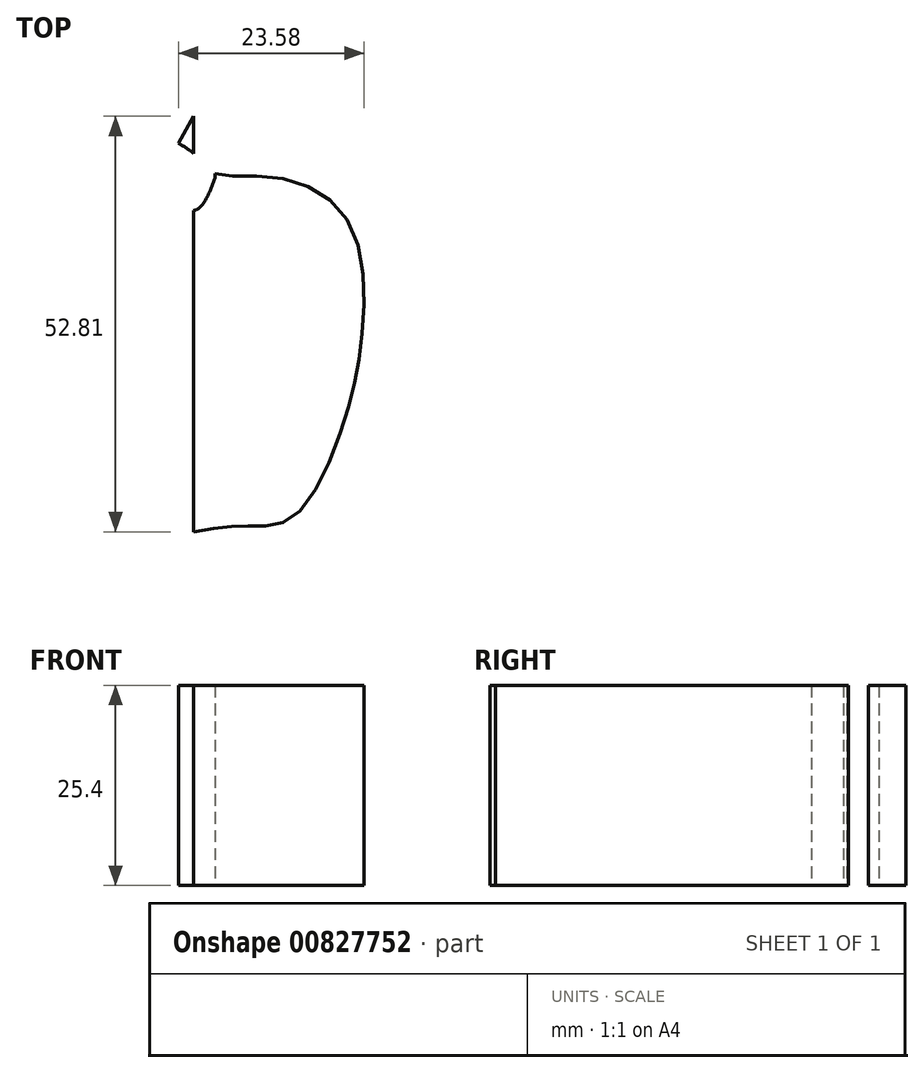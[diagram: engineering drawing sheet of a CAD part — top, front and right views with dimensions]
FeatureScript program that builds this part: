
annotation { "Feature Type Name" : "Feature", "Feature Type Description" : "" }
export const myFeature = defineFeature(function(context is Context, id is Id, definition is map)
    precondition{}
    {
        {
            var Q0;
            Q0=qCreatedBy(makeId("Top.planeOp"),FACE);
            var sketch = newSketch(context, id + "F0", { "sketchPlane" : qUnion([Q0])});
            skLineSegment(sketch, "E0", {"start": v(0, 76.38) * mm, "end": v(0, -76.38) * mm});
            skFitSpline(sketch, "E1", {"points": [v(2.68, 21.15) * mm, v(11.2, 20.52) * mm, v(20.04, 14.2) * mm, v(21.3, 0) * mm, v(19.1, -10.42) * mm, v(12.78, -22.4) * mm, v(7.42, -23.67) * mm, v(2.37, -23.99) * mm, v(-6.15, -24.3) * mm, v(-20.36, -10.73) * mm, v(-23.2, 13.57) * mm, v(-13.73, 20.52) * mm, v(-5.84, 20.52) * mm, v(-7.73, 26.51) * mm, v(0, 23.67) * mm, v(2.68, 21.15) * mm]});
            skFitSpline(sketch, "E2", {"points": [v(-5.84, 20.52) * mm, v(0, 16.41) * mm, v(2.68, 20.52) * mm], "startDerivative": vector(11.98, -12.03) * mm, "endDerivative": vector(4.84, 12.8) * mm});
            skFitSpline(sketch, "E3", {"points": [v(2.68, 21.15) * mm, v(2.68, 20.52) * mm], "startDerivative": vector(0, -0.63) * mm, "endDerivative": vector(0, -0.63) * mm});
            skLineSegment(sketch, "E4", {"start": v(-4.98, 19.66) * mm, "end": v(1.66, 31.34) * mm});
            skLineSegment(sketch, "E5", {"start": v(1.66, 31.34) * mm, "end": v(4.86, 28.96) * mm});
            skLineSegment(sketch, "E6", {"start": v(4.86, 28.96) * mm, "end": v(2.68, 20.94) * mm});
            skSolve(sketch);
        }
        {
            var Q0;
            {var subQ5=sQuery(id+"F0.wireOp",EDGE,"E0");var subQ7=sQuery(id+"F0.wireOp",EDGE,"E1");var subQ8=makeQuery(id+"F0.imprint","INTERSECT",VERTEX,{"derivedFrom":[subQ5,subQ7]});Q0=makeQuery(id+"F0.imprint","IMPRINT",FACE,{"disambiguationData":[TD([[makeQuery(id+"F0.imprint","IMPRINT",EDGE,{"disambiguationData":[TD([[subQ8,1.0]])],"derivedFrom":subQ5}),1.0]])]});}
            var Q1;
            {var subQ0=sQuery(id+"F0.wireOp",EDGE,"E1");var subQ1=sQuery(id+"F0.wireOp",EDGE,"E0");var subQ2=makeQuery(id+"F0.imprint","INTERSECT",VERTEX,{"derivedFrom":[subQ1,subQ0]});Q1=makeQuery(id+"F0.imprint","IMPRINT",FACE,{"disambiguationData":[TD([[makeQuery(id+"F0.imprint","IMPRINT",EDGE,{"disambiguationData":[TD([[subQ2,1.0]])],"derivedFrom":subQ1}),-1.0]])]});}
            extrude(context, id + "F1", {"entities" : qUnion([Q0, Q1]), "depth" : 25.4 * mm, "offsetDistance" : 25.4 * mm});
        }
    });
